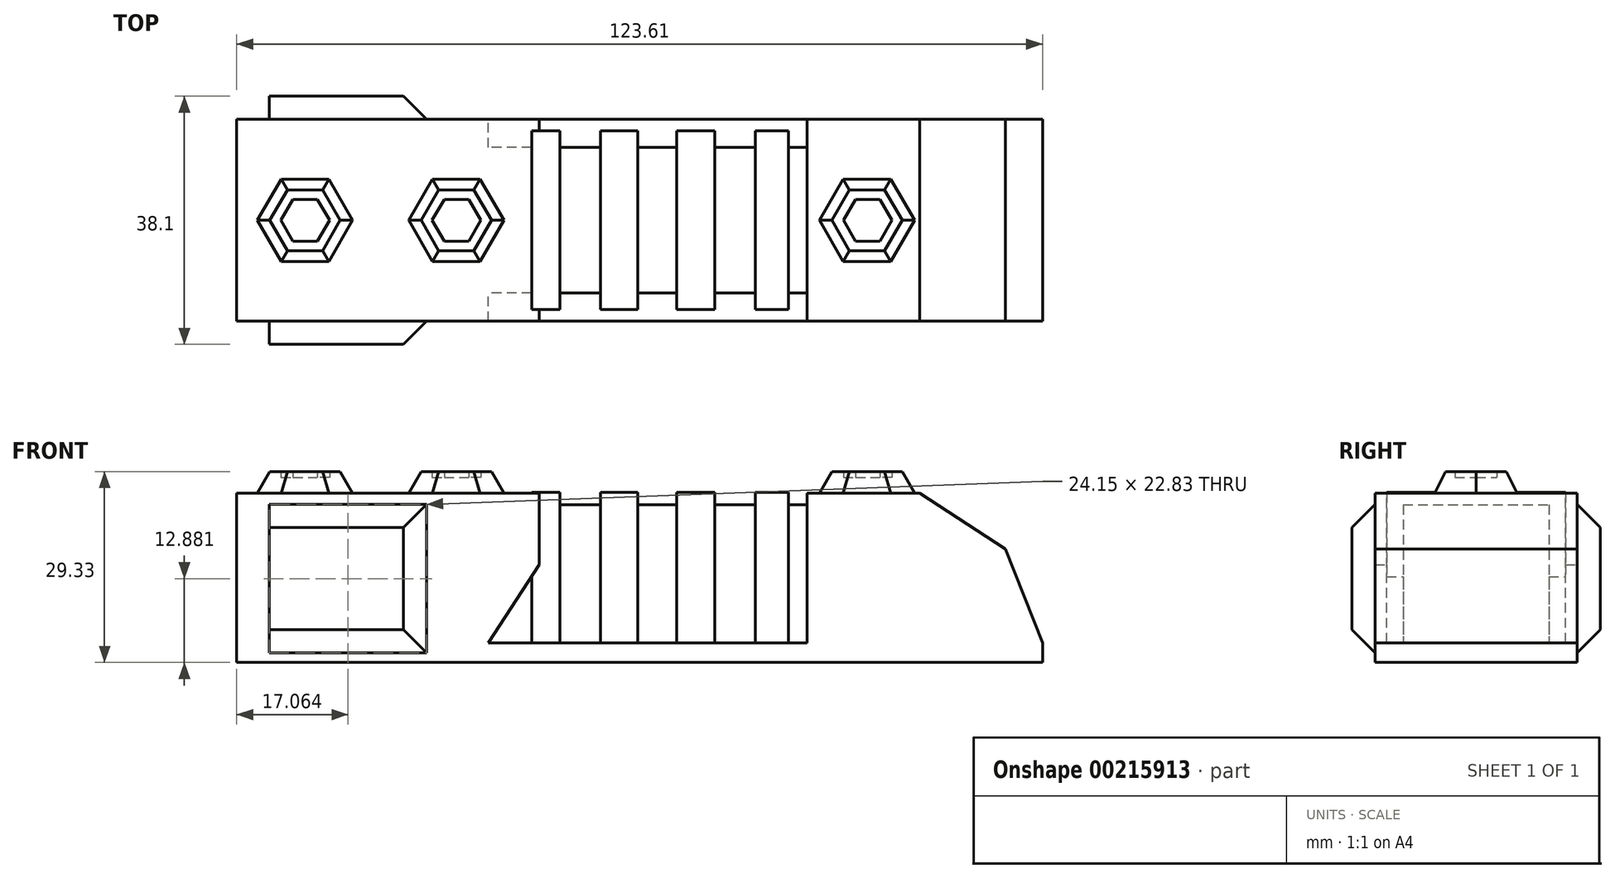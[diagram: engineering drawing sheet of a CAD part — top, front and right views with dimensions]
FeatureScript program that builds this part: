
annotation { "Feature Type Name" : "Feature", "Feature Type Description" : "" }
export const myFeature = defineFeature(function(context is Context, id is Id, definition is map)
    precondition{}
    {
        {
            var Q0;
            Q0=qCreatedBy(makeId("Front.planeOp"),FACE);
            var sketch = newSketch(context, id + "F0", { "sketchPlane" : qUnion([Q0])});
            skLineSegment(sketch, "E0", {"start": v(-61.5, 0) * mm, "end": v(-61.5, 22.99) * mm});
            skLineSegment(sketch, "E1", {"start": v(-61.5, 22.99) * mm, "end": v(-15.07, 22.99) * mm});
            skLineSegment(sketch, "E2", {"start": v(-15.07, 22.99) * mm, "end": v(-15.07, 12) * mm});
            skLineSegment(sketch, "E3", {"start": v(-15.07, 12) * mm, "end": v(-22.92, 0) * mm});
            skLineSegment(sketch, "E4", {"start": v(-22.92, 0) * mm, "end": v(-61.5, 0) * mm});
            skLineSegment(sketch, "E5", {"start": v(25.98, 0) * mm, "end": v(25.98, 22.99) * mm});
            skLineSegment(sketch, "E6", {"start": v(25.98, 22.99) * mm, "end": v(43.26, 22.99) * mm});
            skLineSegment(sketch, "E7", {"start": v(43.26, 22.99) * mm, "end": v(56.42, 14.37) * mm});
            skLineSegment(sketch, "E8", {"start": v(56.42, 14.37) * mm, "end": v(62.1, 0) * mm});
            skLineSegment(sketch, "E9", {"start": v(62.1, 0) * mm, "end": v(25.98, 0) * mm});
            skLineSegment(sketch, "E10", {"start": v(25.98, 0) * mm, "end": v(-22.92, 0) * mm});
            skLineSegment(sketch, "E11", {"start": v(-61.5, 0) * mm, "end": v(-61.5, -3.04) * mm});
            skLineSegment(sketch, "E12", {"start": v(-61.5, -3.04) * mm, "end": v(62.1, -3.04) * mm});
            skLineSegment(sketch, "E13", {"start": v(62.1, -3.04) * mm, "end": v(62.1, 0) * mm});
            skSolve(sketch);
        }
        {
            var Q0;
            Q0 = qSketchRegion(id + "F0", true);
            extrude(context, id + "F1", {"entities" : qUnion([Q0]), "endBound" : BoundingType.SYMMETRIC, "depth" : 30.99 * mm});
        }
        {
            var Q0;
            Q0=qCreatedBy(makeId("Front.planeOp"),FACE);
            var sketch = newSketch(context, id + "F2", { "sketchPlane" : qUnion([Q0])});
            skLineSegment(sketch, "E14.bottom", {"start": v(33.35, 0) * mm, "end": v(-30.42, 0) * mm});
            skLineSegment(sketch, "E14.top", {"start": v(33.35, 21.16) * mm, "end": v(-30.42, 21.16) * mm});
            skLineSegment(sketch, "E14.left", {"start": v(33.35, 0) * mm, "end": v(33.35, 21.16) * mm});
            skLineSegment(sketch, "E14.right", {"start": v(-30.42, 0) * mm, "end": v(-30.42, 21.16) * mm});
            skSolve(sketch);
        }
        {
            var Q0;
            Q0 = qSketchRegion(id + "F2", true);
            extrude(context, id + "F3", {"entities" : qUnion([Q0]), "operationType" : NewBodyOperationType.ADD, "endBound" : BoundingType.SYMMETRIC, "depth" : 22.35 * mm});
        }
        {
            var Q0;
            Q0=qCreatedBy(makeId("Front.planeOp"),FACE);
            var sketch = newSketch(context, id + "F4", { "sketchPlane" : qUnion([Q0])});
            skLineSegment(sketch, "E15.bottom", {"start": v(23.15, 0) * mm, "end": v(18.06, 0) * mm});
            skLineSegment(sketch, "E15.top", {"start": v(23.15, 23.1) * mm, "end": v(18.06, 23.1) * mm});
            skLineSegment(sketch, "E15.left", {"start": v(23.15, 0) * mm, "end": v(23.15, 23.1) * mm});
            skLineSegment(sketch, "E15.right", {"start": v(18.06, 0) * mm, "end": v(18.06, 23.1) * mm});
            skLineSegment(sketch, "E16.bottom", {"start": v(11.83, 0) * mm, "end": v(5.99, 0) * mm});
            skLineSegment(sketch, "E16.top", {"start": v(11.83, 23.1) * mm, "end": v(5.99, 23.1) * mm});
            skLineSegment(sketch, "E16.left", {"start": v(11.83, 0) * mm, "end": v(11.83, 23.1) * mm});
            skLineSegment(sketch, "E16.right", {"start": v(5.99, 0) * mm, "end": v(5.99, 23.1) * mm});
            skLineSegment(sketch, "E17.bottom", {"start": v(0, 0) * mm, "end": v(-5.71, 0) * mm});
            skLineSegment(sketch, "E17.top", {"start": v(0, 23.1) * mm, "end": v(-5.71, 23.1) * mm});
            skLineSegment(sketch, "E17.left", {"start": v(0, 0) * mm, "end": v(0, 23.1) * mm});
            skLineSegment(sketch, "E17.right", {"start": v(-5.71, 0) * mm, "end": v(-5.71, 23.1) * mm});
            skLineSegment(sketch, "E18.bottom", {"start": v(-11.94, 0) * mm, "end": v(-16.27, 0) * mm});
            skLineSegment(sketch, "E18.top", {"start": v(-11.94, 23.1) * mm, "end": v(-16.27, 23.1) * mm});
            skLineSegment(sketch, "E18.left", {"start": v(-11.94, 0) * mm, "end": v(-11.94, 23.1) * mm});
            skLineSegment(sketch, "E18.right", {"start": v(-16.27, 0) * mm, "end": v(-16.27, 23.1) * mm});
            skSolve(sketch);
        }
        {
            var Q0;
            Q0 = qSketchRegion(id + "F4", true);
            extrude(context, id + "F5", {"entities" : qUnion([Q0]), "operationType" : NewBodyOperationType.ADD, "endBound" : BoundingType.SYMMETRIC, "depth" : 27.43 * mm});
        }
        {
            var Q0;
            Q0=qCreatedBy(makeId("Top.planeOp"),FACE);
            var sketch = newSketch(context, id + "F6", { "sketchPlane" : qUnion([Q0])});
            skCircle(sketch, "E19.cCircle", {"center": v(-51.03, 0) * mm, "radius": 3.78 * mm, "construction": true});
            skLineSegment(sketch, "E19.0", {"start": v(-53.21, 3.78) * mm, "end": v(-48.85, 3.78) * mm});
            skLineSegment(sketch, "E19.1", {"start": v(-48.85, 3.78) * mm, "end": v(-46.67, 0) * mm});
            skLineSegment(sketch, "E19.2", {"start": v(-46.67, 0) * mm, "end": v(-48.85, -3.78) * mm});
            skLineSegment(sketch, "E19.3", {"start": v(-48.85, -3.78) * mm, "end": v(-53.21, -3.78) * mm});
            skLineSegment(sketch, "E19.4", {"start": v(-53.21, -3.78) * mm, "end": v(-55.4, 0) * mm});
            skLineSegment(sketch, "E19.5", {"start": v(-55.4, 0) * mm, "end": v(-53.21, 3.78) * mm});
            skPoint(sketch, "E19.0.midPoint", {"position": v(-51.03, 3.78) * mm});
            skCircle(sketch, "E20.cCircle", {"center": v(-27.82, 0) * mm, "radius": 3.78 * mm, "construction": true});
            skLineSegment(sketch, "E20.0", {"start": v(-30, 3.78) * mm, "end": v(-25.64, 3.78) * mm});
            skLineSegment(sketch, "E20.1", {"start": v(-25.64, 3.78) * mm, "end": v(-23.46, 0) * mm});
            skLineSegment(sketch, "E20.2", {"start": v(-23.46, 0) * mm, "end": v(-25.64, -3.78) * mm});
            skLineSegment(sketch, "E20.3", {"start": v(-25.64, -3.78) * mm, "end": v(-30, -3.78) * mm});
            skLineSegment(sketch, "E20.4", {"start": v(-30, -3.78) * mm, "end": v(-32.18, 0) * mm});
            skLineSegment(sketch, "E20.5", {"start": v(-32.18, 0) * mm, "end": v(-30, 3.78) * mm});
            skPoint(sketch, "E20.0.midPoint", {"position": v(-27.82, 3.78) * mm});
            skCircle(sketch, "E21.cCircle", {"center": v(35.17, 0) * mm, "radius": 3.78 * mm, "construction": true});
            skLineSegment(sketch, "E21.0", {"start": v(32.98, 3.78) * mm, "end": v(37.35, 3.78) * mm});
            skLineSegment(sketch, "E21.1", {"start": v(37.35, 3.78) * mm, "end": v(39.53, 0) * mm});
            skLineSegment(sketch, "E21.2", {"start": v(39.53, 0) * mm, "end": v(37.35, -3.78) * mm});
            skLineSegment(sketch, "E21.3", {"start": v(37.35, -3.78) * mm, "end": v(32.98, -3.78) * mm});
            skLineSegment(sketch, "E21.4", {"start": v(32.98, -3.78) * mm, "end": v(30.8, 0) * mm});
            skLineSegment(sketch, "E21.5", {"start": v(30.8, 0) * mm, "end": v(32.98, 3.78) * mm});
            skPoint(sketch, "E21.0.midPoint", {"position": v(35.17, 3.78) * mm});
            skSolve(sketch);
        }
        {
            var Q0;
            Q0 = qSketchRegion(id + "F6", true);
            extrude(context, id + "F7", {"entities" : qUnion([Q0]), "operationType" : NewBodyOperationType.ADD, "depth" : 26.29 * mm});
        }
        {
            var Q0;
            Q0=makeQuery(id+"F7.boolean.opBoolean","INTERSECT",EDGE,{"derivedFrom":[makeQuery(id+"F1.opExtrude","SWEPT_FACE",FACE,{"disambiguationData":[OSD([sQuery(id+"F0.wireOp",EDGE,"E1")])]}),makeQuery(id+"F7.opExtrude","SWEPT_FACE",FACE,{"disambiguationData":[OSD([sQuery(id+"F6.wireOp",EDGE,"E19.3")])]})]});
            var Q1;
            Q1=makeQuery(id+"F7.boolean.opBoolean","INTERSECT",EDGE,{"derivedFrom":[makeQuery(id+"F1.opExtrude","SWEPT_FACE",FACE,{"disambiguationData":[OSD([sQuery(id+"F0.wireOp",EDGE,"E1")])]}),makeQuery(id+"F7.opExtrude","SWEPT_FACE",FACE,{"disambiguationData":[OSD([sQuery(id+"F6.wireOp",EDGE,"E19.2")])]})]});
            var Q2;
            Q2=makeQuery(id+"F7.boolean.opBoolean","INTERSECT",EDGE,{"derivedFrom":[makeQuery(id+"F1.opExtrude","SWEPT_FACE",FACE,{"disambiguationData":[OSD([sQuery(id+"F0.wireOp",EDGE,"E1")])]}),makeQuery(id+"F7.opExtrude","SWEPT_FACE",FACE,{"disambiguationData":[OSD([sQuery(id+"F6.wireOp",EDGE,"E19.4")])]})]});
            var Q3;
            Q3=makeQuery(id+"F7.boolean.opBoolean","INTERSECT",EDGE,{"derivedFrom":[makeQuery(id+"F1.opExtrude","SWEPT_FACE",FACE,{"disambiguationData":[OSD([sQuery(id+"F0.wireOp",EDGE,"E1")])]}),makeQuery(id+"F7.opExtrude","SWEPT_FACE",FACE,{"disambiguationData":[OSD([sQuery(id+"F6.wireOp",EDGE,"E19.0")])]})]});
            var Q4;
            Q4=makeQuery(id+"F7.boolean.opBoolean","INTERSECT",EDGE,{"derivedFrom":[makeQuery(id+"F1.opExtrude","SWEPT_FACE",FACE,{"disambiguationData":[OSD([sQuery(id+"F0.wireOp",EDGE,"E1")])]}),makeQuery(id+"F7.opExtrude","SWEPT_FACE",FACE,{"disambiguationData":[OSD([sQuery(id+"F6.wireOp",EDGE,"E19.1")])]})]});
            var Q5;
            Q5=makeQuery(id+"F7.boolean.opBoolean","INTERSECT",EDGE,{"derivedFrom":[makeQuery(id+"F1.opExtrude","SWEPT_FACE",FACE,{"disambiguationData":[OSD([sQuery(id+"F0.wireOp",EDGE,"E1")])]}),makeQuery(id+"F7.opExtrude","SWEPT_FACE",FACE,{"disambiguationData":[OSD([sQuery(id+"F6.wireOp",EDGE,"E20.3")])]})]});
            var Q6;
            Q6=makeQuery(id+"F7.boolean.opBoolean","INTERSECT",EDGE,{"derivedFrom":[makeQuery(id+"F1.opExtrude","SWEPT_FACE",FACE,{"disambiguationData":[OSD([sQuery(id+"F0.wireOp",EDGE,"E1")])]}),makeQuery(id+"F7.opExtrude","SWEPT_FACE",FACE,{"disambiguationData":[OSD([sQuery(id+"F6.wireOp",EDGE,"E20.4")])]})]});
            var Q7;
            Q7=makeQuery(id+"F7.boolean.opBoolean","INTERSECT",EDGE,{"derivedFrom":[makeQuery(id+"F1.opExtrude","SWEPT_FACE",FACE,{"disambiguationData":[OSD([sQuery(id+"F0.wireOp",EDGE,"E1")])]}),makeQuery(id+"F7.opExtrude","SWEPT_FACE",FACE,{"disambiguationData":[OSD([sQuery(id+"F6.wireOp",EDGE,"E20.5")])]})]});
            var Q8;
            Q8=makeQuery(id+"F7.boolean.opBoolean","INTERSECT",EDGE,{"derivedFrom":[makeQuery(id+"F1.opExtrude","SWEPT_FACE",FACE,{"disambiguationData":[OSD([sQuery(id+"F0.wireOp",EDGE,"E1")])]}),makeQuery(id+"F7.opExtrude","SWEPT_FACE",FACE,{"disambiguationData":[OSD([sQuery(id+"F6.wireOp",EDGE,"E20.0")])]})]});
            var Q9;
            Q9=makeQuery(id+"F7.boolean.opBoolean","INTERSECT",EDGE,{"derivedFrom":[makeQuery(id+"F1.opExtrude","SWEPT_FACE",FACE,{"disambiguationData":[OSD([sQuery(id+"F0.wireOp",EDGE,"E1")])]}),makeQuery(id+"F7.opExtrude","SWEPT_FACE",FACE,{"disambiguationData":[OSD([sQuery(id+"F6.wireOp",EDGE,"E20.1")])]})]});
            var Q10;
            Q10=makeQuery(id+"F7.boolean.opBoolean","INTERSECT",EDGE,{"derivedFrom":[makeQuery(id+"F1.opExtrude","SWEPT_FACE",FACE,{"disambiguationData":[OSD([sQuery(id+"F0.wireOp",EDGE,"E1")])]}),makeQuery(id+"F7.opExtrude","SWEPT_FACE",FACE,{"disambiguationData":[OSD([sQuery(id+"F6.wireOp",EDGE,"E20.2")])]})]});
            var Q11;
            Q11=makeQuery(id+"F7.boolean.opBoolean","INTERSECT",EDGE,{"derivedFrom":[makeQuery(id+"F1.opExtrude","SWEPT_FACE",FACE,{"disambiguationData":[OSD([sQuery(id+"F0.wireOp",EDGE,"E1")])]}),makeQuery(id+"F7.opExtrude","SWEPT_FACE",FACE,{"disambiguationData":[OSD([sQuery(id+"F6.wireOp",EDGE,"E19.5")])]})]});
            chamfer(context, id + "F8", {"entities" : qUnion([Q0, Q1, Q2, Q3, Q4, Q5, Q6, Q7, Q8, Q9, Q10, Q11]), "chamferType" : ChamferType.TWO_OFFSETS, "width1" : 5.08 * mm, "oppositeDirection" : false, "width2" : 2.54 * mm, "tangentPropagation" : true});
        }
        {
            var Q0;
            Q0=qCreatedBy(makeId("Top.planeOp"),FACE);
            var sketch = newSketch(context, id + "F9", { "sketchPlane" : qUnion([Q0])});
            skCircle(sketch, "E22.cCircle", {"center": v(-51, 0) * mm, "radius": 3.23 * mm, "construction": true});
            skLineSegment(sketch, "E22.0", {"start": v(-52.86, 3.23) * mm, "end": v(-49.13, 3.23) * mm});
            skLineSegment(sketch, "E22.1", {"start": v(-49.13, 3.23) * mm, "end": v(-47.26, 0) * mm});
            skLineSegment(sketch, "E22.2", {"start": v(-47.26, 0) * mm, "end": v(-49.13, -3.23) * mm});
            skLineSegment(sketch, "E22.3", {"start": v(-49.13, -3.23) * mm, "end": v(-52.86, -3.23) * mm});
            skLineSegment(sketch, "E22.4", {"start": v(-52.86, -3.23) * mm, "end": v(-54.73, 0) * mm});
            skLineSegment(sketch, "E22.5", {"start": v(-54.73, 0) * mm, "end": v(-52.86, 3.23) * mm});
            skPoint(sketch, "E22.0.midPoint", {"position": v(-51, 3.23) * mm});
            skCircle(sketch, "E23.cCircle", {"center": v(-27.8, 0) * mm, "radius": 3.23 * mm, "construction": true});
            skLineSegment(sketch, "E23.0", {"start": v(-29.66, 3.23) * mm, "end": v(-25.92, 3.23) * mm});
            skLineSegment(sketch, "E23.1", {"start": v(-25.92, 3.23) * mm, "end": v(-24.06, 0) * mm});
            skLineSegment(sketch, "E23.2", {"start": v(-24.06, 0) * mm, "end": v(-25.92, -3.23) * mm});
            skLineSegment(sketch, "E23.3", {"start": v(-25.92, -3.23) * mm, "end": v(-29.66, -3.23) * mm});
            skLineSegment(sketch, "E23.4", {"start": v(-29.66, -3.23) * mm, "end": v(-31.52, 0) * mm});
            skLineSegment(sketch, "E23.5", {"start": v(-31.52, 0) * mm, "end": v(-29.66, 3.23) * mm});
            skPoint(sketch, "E23.0.midPoint", {"position": v(-27.8, 3.23) * mm});
            skCircle(sketch, "E24.cCircle", {"center": v(35.3, 0) * mm, "radius": 3.23 * mm, "construction": true});
            skLineSegment(sketch, "E24.0", {"start": v(33.42, 3.23) * mm, "end": v(37.16, 3.23) * mm});
            skLineSegment(sketch, "E24.1", {"start": v(37.16, 3.23) * mm, "end": v(39.03, 0) * mm});
            skLineSegment(sketch, "E24.2", {"start": v(39.03, 0) * mm, "end": v(37.16, -3.23) * mm});
            skLineSegment(sketch, "E24.3", {"start": v(37.16, -3.23) * mm, "end": v(33.42, -3.23) * mm});
            skLineSegment(sketch, "E24.4", {"start": v(33.42, -3.23) * mm, "end": v(31.56, 0) * mm});
            skLineSegment(sketch, "E24.5", {"start": v(31.56, 0) * mm, "end": v(33.42, 3.23) * mm});
            skPoint(sketch, "E24.0.midPoint", {"position": v(35.3, 3.23) * mm});
            skSolve(sketch);
        }
        {
            var Q0;
            Q0 = qSketchRegion(id + "F9", true);
            extrude(context, id + "F10", {"entities" : qUnion([Q0]), "operationType" : NewBodyOperationType.REMOVE, "depth" : 51.05 * mm});
        }
        {
            var Q0;
            Q0=qCreatedBy(makeId("Front.planeOp"),FACE);
            var sketch = newSketch(context, id + "F11", { "sketchPlane" : qUnion([Q0])});
            skLineSegment(sketch, "E25.bottom", {"start": v(-56.52, 16.18) * mm, "end": v(-37.45, 16.18) * mm});
            skLineSegment(sketch, "E25.top", {"start": v(-56.52, 3.5) * mm, "end": v(-37.45, 3.5) * mm});
            skLineSegment(sketch, "E25.left", {"start": v(-56.52, 16.18) * mm, "end": v(-56.52, 3.5) * mm});
            skLineSegment(sketch, "E25.right", {"start": v(-37.45, 16.18) * mm, "end": v(-37.45, 3.5) * mm});
            skSolve(sketch);
        }
        {
            var Q0;
            Q0 = qSketchRegion(id + "F11", true);
            extrude(context, id + "F12", {"entities" : qUnion([Q0]), "operationType" : NewBodyOperationType.ADD, "endBound" : BoundingType.SYMMETRIC, "depth" : 38.1 * mm});
        }
        {
            var Q0;
            Q0=makeQuery(id+"F12.boolean.opBoolean","INTERSECT",EDGE,{"derivedFrom":[makeQuery(id+"F1.opExtrude","CAP_FACE",FACE,{"disambiguationData":[OSD([sQuery(id+"F0.wireOp",EDGE,"E0"),sQuery(id+"F0.wireOp",EDGE,"E1"),sQuery(id+"F0.wireOp",EDGE,"E2"),sQuery(id+"F0.wireOp",EDGE,"E3"),sQuery(id+"F0.wireOp",EDGE,"E5"),sQuery(id+"F0.wireOp",EDGE,"E6"),sQuery(id+"F0.wireOp",EDGE,"E7"),sQuery(id+"F0.wireOp",EDGE,"E8"),sQuery(id+"F0.wireOp",EDGE,"E10"),sQuery(id+"F0.wireOp",EDGE,"E11"),sQuery(id+"F0.wireOp",EDGE,"E12"),sQuery(id+"F0.wireOp",EDGE,"E13")])],"isStart":false}),makeQuery(id+"F12.opExtrude","SWEPT_FACE",FACE,{"disambiguationData":[OSD([sQuery(id+"F11.wireOp",EDGE,"E25.top")])]})]});
            var Q1;
            Q1=makeQuery(id+"F12.boolean.opBoolean","INTERSECT",EDGE,{"derivedFrom":[makeQuery(id+"F1.opExtrude","CAP_FACE",FACE,{"disambiguationData":[OSD([sQuery(id+"F0.wireOp",EDGE,"E0"),sQuery(id+"F0.wireOp",EDGE,"E1"),sQuery(id+"F0.wireOp",EDGE,"E2"),sQuery(id+"F0.wireOp",EDGE,"E3"),sQuery(id+"F0.wireOp",EDGE,"E5"),sQuery(id+"F0.wireOp",EDGE,"E6"),sQuery(id+"F0.wireOp",EDGE,"E7"),sQuery(id+"F0.wireOp",EDGE,"E8"),sQuery(id+"F0.wireOp",EDGE,"E10"),sQuery(id+"F0.wireOp",EDGE,"E11"),sQuery(id+"F0.wireOp",EDGE,"E12"),sQuery(id+"F0.wireOp",EDGE,"E13")])],"isStart":false}),makeQuery(id+"F12.opExtrude","SWEPT_FACE",FACE,{"disambiguationData":[OSD([sQuery(id+"F11.wireOp",EDGE,"E25.right")])]})]});
            var Q2;
            Q2=makeQuery(id+"F12.boolean.opBoolean","INTERSECT",EDGE,{"derivedFrom":[makeQuery(id+"F1.opExtrude","CAP_FACE",FACE,{"disambiguationData":[OSD([sQuery(id+"F0.wireOp",EDGE,"E0"),sQuery(id+"F0.wireOp",EDGE,"E1"),sQuery(id+"F0.wireOp",EDGE,"E2"),sQuery(id+"F0.wireOp",EDGE,"E3"),sQuery(id+"F0.wireOp",EDGE,"E5"),sQuery(id+"F0.wireOp",EDGE,"E6"),sQuery(id+"F0.wireOp",EDGE,"E7"),sQuery(id+"F0.wireOp",EDGE,"E8"),sQuery(id+"F0.wireOp",EDGE,"E10"),sQuery(id+"F0.wireOp",EDGE,"E11"),sQuery(id+"F0.wireOp",EDGE,"E12"),sQuery(id+"F0.wireOp",EDGE,"E13")])],"isStart":false}),makeQuery(id+"F12.opExtrude","SWEPT_FACE",FACE,{"disambiguationData":[OSD([sQuery(id+"F11.wireOp",EDGE,"E25.bottom")])]})]});
            var Q3;
            Q3=makeQuery(id+"F12.boolean.opBoolean","INTERSECT",EDGE,{"derivedFrom":[makeQuery(id+"F1.opExtrude","CAP_FACE",FACE,{"disambiguationData":[OSD([sQuery(id+"F0.wireOp",EDGE,"E0"),sQuery(id+"F0.wireOp",EDGE,"E1"),sQuery(id+"F0.wireOp",EDGE,"E2"),sQuery(id+"F0.wireOp",EDGE,"E3"),sQuery(id+"F0.wireOp",EDGE,"E5"),sQuery(id+"F0.wireOp",EDGE,"E6"),sQuery(id+"F0.wireOp",EDGE,"E7"),sQuery(id+"F0.wireOp",EDGE,"E8"),sQuery(id+"F0.wireOp",EDGE,"E10"),sQuery(id+"F0.wireOp",EDGE,"E11"),sQuery(id+"F0.wireOp",EDGE,"E12"),sQuery(id+"F0.wireOp",EDGE,"E13")])],"isStart":true}),makeQuery(id+"F12.opExtrude","SWEPT_FACE",FACE,{"disambiguationData":[OSD([sQuery(id+"F11.wireOp",EDGE,"E25.top")])]})]});
            var Q4;
            Q4=makeQuery(id+"F12.boolean.opBoolean","INTERSECT",EDGE,{"derivedFrom":[makeQuery(id+"F1.opExtrude","CAP_FACE",FACE,{"disambiguationData":[OSD([sQuery(id+"F0.wireOp",EDGE,"E0"),sQuery(id+"F0.wireOp",EDGE,"E1"),sQuery(id+"F0.wireOp",EDGE,"E2"),sQuery(id+"F0.wireOp",EDGE,"E3"),sQuery(id+"F0.wireOp",EDGE,"E5"),sQuery(id+"F0.wireOp",EDGE,"E6"),sQuery(id+"F0.wireOp",EDGE,"E7"),sQuery(id+"F0.wireOp",EDGE,"E8"),sQuery(id+"F0.wireOp",EDGE,"E10"),sQuery(id+"F0.wireOp",EDGE,"E11"),sQuery(id+"F0.wireOp",EDGE,"E12"),sQuery(id+"F0.wireOp",EDGE,"E13")])],"isStart":true}),makeQuery(id+"F12.opExtrude","SWEPT_FACE",FACE,{"disambiguationData":[OSD([sQuery(id+"F11.wireOp",EDGE,"E25.right")])]})]});
            var Q5;
            Q5=makeQuery(id+"F12.boolean.opBoolean","INTERSECT",EDGE,{"derivedFrom":[makeQuery(id+"F1.opExtrude","CAP_FACE",FACE,{"disambiguationData":[OSD([sQuery(id+"F0.wireOp",EDGE,"E0"),sQuery(id+"F0.wireOp",EDGE,"E1"),sQuery(id+"F0.wireOp",EDGE,"E2"),sQuery(id+"F0.wireOp",EDGE,"E3"),sQuery(id+"F0.wireOp",EDGE,"E5"),sQuery(id+"F0.wireOp",EDGE,"E6"),sQuery(id+"F0.wireOp",EDGE,"E7"),sQuery(id+"F0.wireOp",EDGE,"E8"),sQuery(id+"F0.wireOp",EDGE,"E10"),sQuery(id+"F0.wireOp",EDGE,"E11"),sQuery(id+"F0.wireOp",EDGE,"E12"),sQuery(id+"F0.wireOp",EDGE,"E13")])],"isStart":true}),makeQuery(id+"F12.opExtrude","SWEPT_FACE",FACE,{"disambiguationData":[OSD([sQuery(id+"F11.wireOp",EDGE,"E25.bottom")])]})]});
            chamfer(context, id + "F13", {"entities" : qUnion([Q0, Q1, Q2, Q3, Q4, Q5]), "width" : 5.08 * mm, "tangentPropagation" : true});
        }
        {
            var Q0;
            Q0=makeQuery(id+"F7.boolean.opBoolean","INTERSECT",EDGE,{"derivedFrom":[makeQuery(id+"F1.opExtrude","SWEPT_FACE",FACE,{"disambiguationData":[OSD([sQuery(id+"F0.wireOp",EDGE,"E6")])]}),makeQuery(id+"F7.opExtrude","SWEPT_FACE",FACE,{"disambiguationData":[OSD([sQuery(id+"F6.wireOp",EDGE,"E21.3")])]})]});
            var Q1;
            Q1=makeQuery(id+"F7.boolean.opBoolean","INTERSECT",EDGE,{"derivedFrom":[makeQuery(id+"F1.opExtrude","SWEPT_FACE",FACE,{"disambiguationData":[OSD([sQuery(id+"F0.wireOp",EDGE,"E6")])]}),makeQuery(id+"F7.opExtrude","SWEPT_FACE",FACE,{"disambiguationData":[OSD([sQuery(id+"F6.wireOp",EDGE,"E21.4")])]})]});
            var Q2;
            Q2=makeQuery(id+"F7.boolean.opBoolean","INTERSECT",EDGE,{"derivedFrom":[makeQuery(id+"F1.opExtrude","SWEPT_FACE",FACE,{"disambiguationData":[OSD([sQuery(id+"F0.wireOp",EDGE,"E6")])]}),makeQuery(id+"F7.opExtrude","SWEPT_FACE",FACE,{"disambiguationData":[OSD([sQuery(id+"F6.wireOp",EDGE,"E21.2")])]})]});
            var Q3;
            Q3=makeQuery(id+"F7.boolean.opBoolean","INTERSECT",EDGE,{"derivedFrom":[makeQuery(id+"F1.opExtrude","SWEPT_FACE",FACE,{"disambiguationData":[OSD([sQuery(id+"F0.wireOp",EDGE,"E6")])]}),makeQuery(id+"F7.opExtrude","SWEPT_FACE",FACE,{"disambiguationData":[OSD([sQuery(id+"F6.wireOp",EDGE,"E21.5")])]})]});
            var Q4;
            Q4=makeQuery(id+"F7.boolean.opBoolean","INTERSECT",EDGE,{"derivedFrom":[makeQuery(id+"F1.opExtrude","SWEPT_FACE",FACE,{"disambiguationData":[OSD([sQuery(id+"F0.wireOp",EDGE,"E6")])]}),makeQuery(id+"F7.opExtrude","SWEPT_FACE",FACE,{"disambiguationData":[OSD([sQuery(id+"F6.wireOp",EDGE,"E21.0")])]})]});
            var Q5;
            Q5=makeQuery(id+"F7.boolean.opBoolean","INTERSECT",EDGE,{"derivedFrom":[makeQuery(id+"F1.opExtrude","SWEPT_FACE",FACE,{"disambiguationData":[OSD([sQuery(id+"F0.wireOp",EDGE,"E6")])]}),makeQuery(id+"F7.opExtrude","SWEPT_FACE",FACE,{"disambiguationData":[OSD([sQuery(id+"F6.wireOp",EDGE,"E21.1")])]})]});
            chamfer(context, id + "F14", {"entities" : qUnion([Q0, Q1, Q2, Q3, Q4, Q5]), "chamferType" : ChamferType.TWO_OFFSETS, "width1" : 5.08 * mm, "oppositeDirection" : false, "width2" : 2.54 * mm, "tangentPropagation" : true});
        }
        {
            var Q0;
            Q0 = qSketchRegion(id + "F9", true);
            extrude(context, id + "F15", {"entities" : qUnion([Q0]), "operationType" : NewBodyOperationType.ADD, "depth" : 25.4 * mm});
        }
    });
